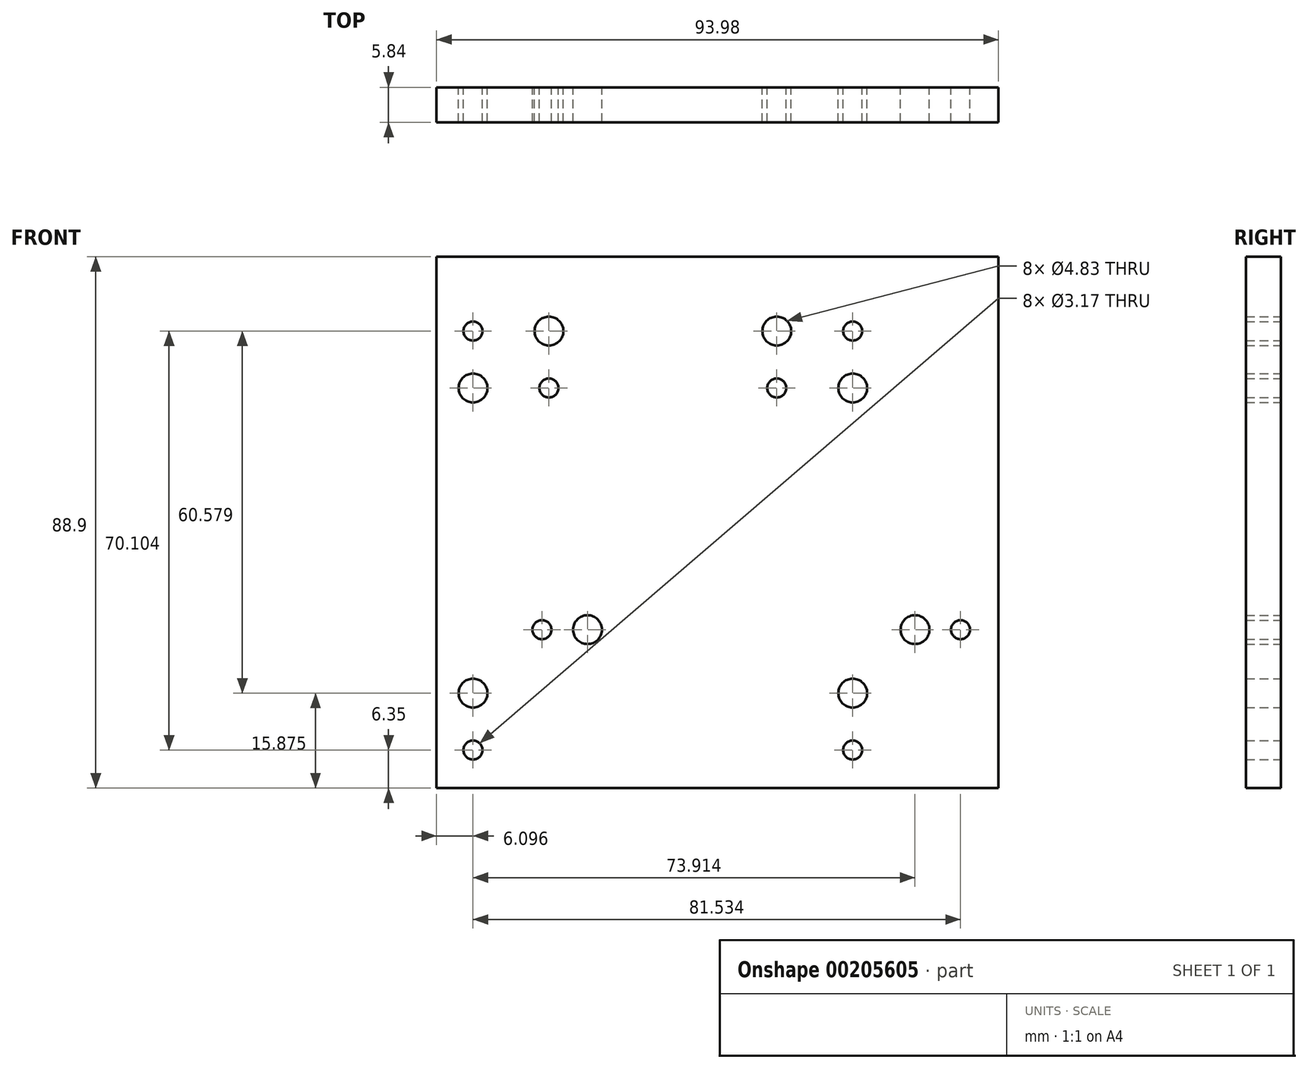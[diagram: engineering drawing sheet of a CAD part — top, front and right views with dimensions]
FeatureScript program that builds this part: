
annotation { "Feature Type Name" : "Feature", "Feature Type Description" : "" }
export const myFeature = defineFeature(function(context is Context, id is Id, definition is map)
    precondition{}
    {
        {
            var Q0;
            Q0=qCreatedBy(makeId("Front.planeOp"),FACE);
            var sketch = newSketch(context, id + "F0", { "sketchPlane" : qUnion([Q0])});
            skLineSegment(sketch, "E0", {"start": v(0, 0) * mm, "end": v(93.98, 0) * mm});
            skLineSegment(sketch, "E1", {"start": v(93.98, -88.9) * mm, "end": v(0, -88.9) * mm});
            skLineSegment(sketch, "E2", {"start": v(0, -88.9) * mm, "end": v(0, 0) * mm});
            skCircle(sketch, "E3", {"center": v(18.8, -12.45) * mm, "radius": 2.41 * mm});
            skCircle(sketch, "E4", {"center": v(56.9, -12.45) * mm, "radius": 2.41 * mm});
            skCircle(sketch, "E5", {"center": v(18.8, -21.97) * mm, "radius": 1.59 * mm});
            skCircle(sketch, "E6", {"center": v(56.9, -21.97) * mm, "radius": 1.59 * mm});
            skCircle(sketch, "E7", {"center": v(69.6, -12.45) * mm, "radius": 1.59 * mm});
            skCircle(sketch, "E8", {"center": v(69.6, -21.97) * mm, "radius": 2.41 * mm});
            skCircle(sketch, "E9", {"center": v(6.1, -12.45) * mm, "radius": 1.59 * mm});
            skCircle(sketch, "E10", {"center": v(6.1, -21.97) * mm, "radius": 2.41 * mm});
            skCircle(sketch, "E11", {"center": v(6.1, -73.03) * mm, "radius": 2.41 * mm});
            skCircle(sketch, "E12", {"center": v(6.1, -82.55) * mm, "radius": 1.59 * mm});
            skCircle(sketch, "E13", {"center": v(69.6, -73.03) * mm, "radius": 2.41 * mm});
            skCircle(sketch, "E14", {"center": v(69.6, -82.55) * mm, "radius": 1.59 * mm});
            skCircle(sketch, "E15", {"center": v(17.63, -62.4) * mm, "radius": 1.59 * mm});
            skCircle(sketch, "E16", {"center": v(25.25, -62.4) * mm, "radius": 2.41 * mm});
            skCircle(sketch, "E17", {"center": v(80.01, -62.4) * mm, "radius": 2.41 * mm});
            skCircle(sketch, "E18", {"center": v(87.63, -62.4) * mm, "radius": 1.59 * mm});
            skLineSegment(sketch, "E19", {"start": v(93.98, 0) * mm, "end": v(93.98, -88.9) * mm});
            skSolve(sketch);
        }
        {
            var Q0;
            Q0=qSketchRegion(id+"F0",true);
            extrude(context, id + "F1", {"entities" : qUnion([Q0]), "depth" : 5.84 * mm});
        }
    });
